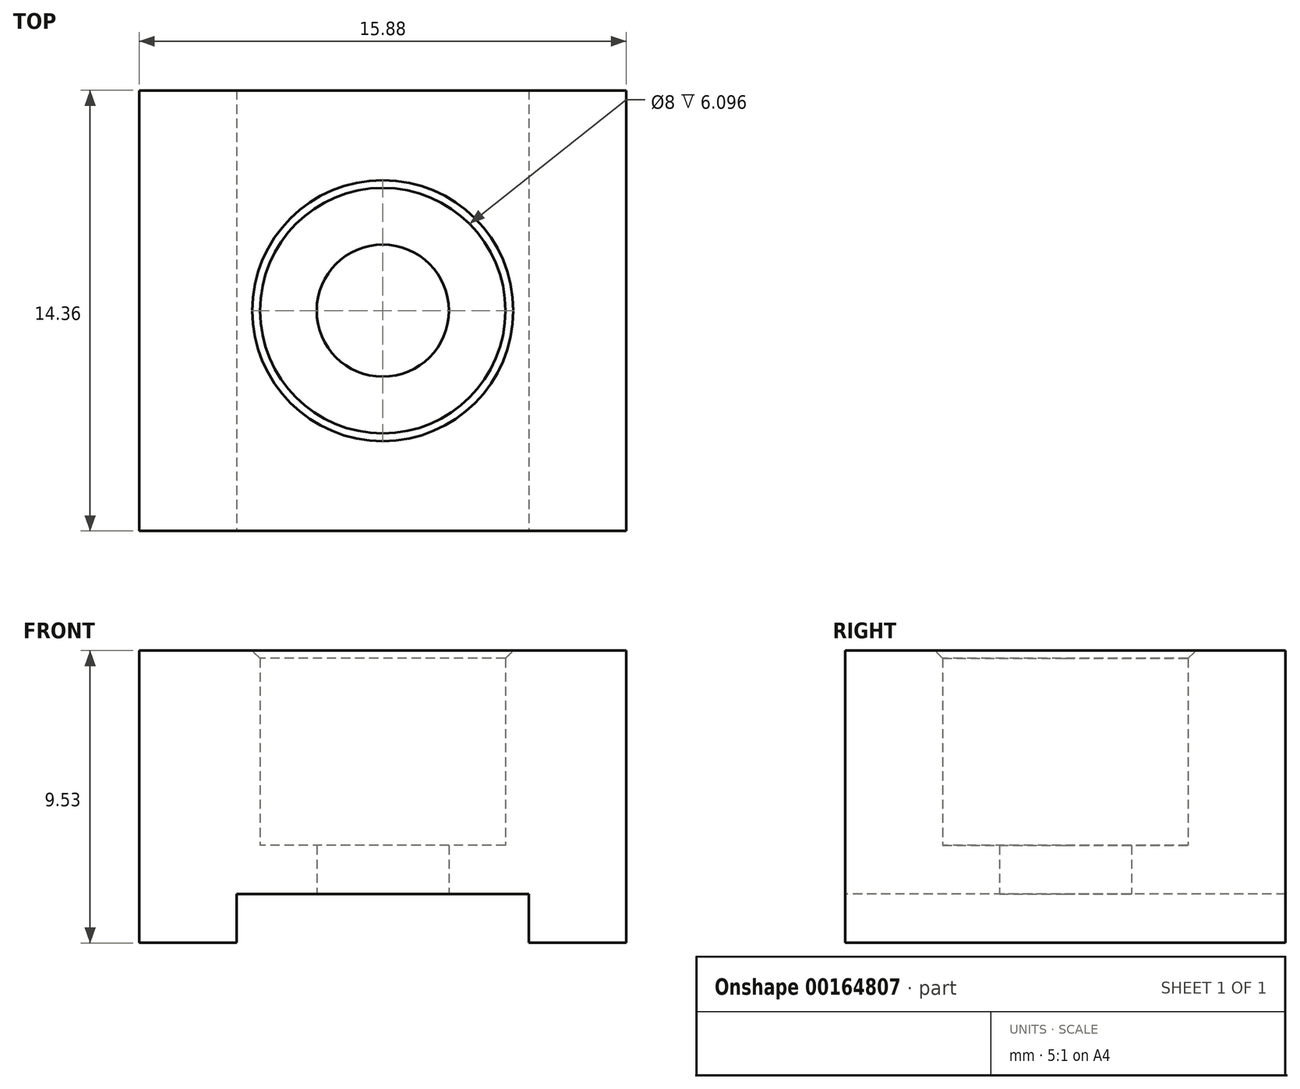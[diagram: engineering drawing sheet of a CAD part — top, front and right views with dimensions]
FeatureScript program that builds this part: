
annotation { "Feature Type Name" : "Feature", "Feature Type Description" : "" }
export const myFeature = defineFeature(function(context is Context, id is Id, definition is map)
    precondition{}
    {
        {
            var Q0;
            Q0=qCreatedBy(makeId("Top.planeOp"),FACE);
            var sketch = newSketch(context, id + "F0", { "sketchPlane" : qUnion([Q0])});
            skLineSegment(sketch, "E0.bottom", {"start": v(7.94, 7.18) * mm, "end": v(-7.94, 7.18) * mm});
            skLineSegment(sketch, "E0.top", {"start": v(7.94, -7.18) * mm, "end": v(-7.94, -7.18) * mm});
            skLineSegment(sketch, "E0.left", {"start": v(7.94, 7.18) * mm, "end": v(7.94, -7.18) * mm});
            skLineSegment(sketch, "E0.right", {"start": v(-7.94, 7.18) * mm, "end": v(-7.94, -7.18) * mm});
            skPoint(sketch, "E0.middle", {"position": v(0, 0) * mm});
            skCircle(sketch, "E1", {"center": v(0, 0) * mm, "radius": 2.15 * mm});
            skSolve(sketch);
        }
        {
            var Q0;
            Q0 = qSketchRegion(id + "F0", true);
            extrude(context, id + "F1", {"entities" : qUnion([Q0]), "depth" : 1.59 * mm});
        }
        {
            var Q0;
            Q0=makeQuery(id+"F1.opExtrude","CAP_FACE",FACE,{"disambiguationData":[OSD([sQuery(id+"F0.wireOp",EDGE,"E0.bottom"),sQuery(id+"F0.wireOp",EDGE,"E0.top"),sQuery(id+"F0.wireOp",EDGE,"E0.left"),sQuery(id+"F0.wireOp",EDGE,"E0.right"),sQuery(id+"F0.wireOp",EDGE,"E1")])],"isStart":false});
            var sketch = newSketch(context, id + "F2", { "sketchPlane" : qUnion([Q0])});
            skCircle(sketch, "E2", {"center": v(0, 0) * mm, "radius": 4 * mm});
            skLineSegment(sketch, "E3.bottom", {"start": v(-7.94, -7.18) * mm, "end": v(7.94, -7.18) * mm});
            skLineSegment(sketch, "E3.top", {"start": v(-7.94, 7.18) * mm, "end": v(7.94, 7.18) * mm});
            skLineSegment(sketch, "E3.left", {"start": v(-7.94, -7.18) * mm, "end": v(-7.94, 7.18) * mm});
            skLineSegment(sketch, "E3.right", {"start": v(7.94, -7.18) * mm, "end": v(7.94, 7.18) * mm});
            skSolve(sketch);
        }
        {
            var Q0;
            Q0 = qSketchRegion(id + "F2", true);
            extrude(context, id + "F3", {"entities" : qUnion([Q0]), "operationType" : NewBodyOperationType.ADD, "depth" : 6.35 * mm});
        }
        {
            var Q0;
            Q0=makeQuery(id+"F3.opExtrude","CAP_EDGE",EDGE,{"disambiguationData":[OSD([sQuery(id+"F2.wireOp",EDGE,"E2")])],"isStart":false});
            chamfer(context, id + "F4", {"entities" : qUnion([Q0]), "width" : 0.25 * mm, "tangentPropagation" : true});
        }
        {
            var Q0;
            Q0=makeQuery(id+"F1.opExtrude","CAP_FACE",FACE,{"disambiguationData":[OSD([sQuery(id+"F0.wireOp",EDGE,"E0.bottom"),sQuery(id+"F0.wireOp",EDGE,"E0.top"),sQuery(id+"F0.wireOp",EDGE,"E0.left"),sQuery(id+"F0.wireOp",EDGE,"E0.right"),sQuery(id+"F0.wireOp",EDGE,"E1")])],"isStart":true});
            var sketch = newSketch(context, id + "F5", { "sketchPlane" : qUnion([Q0])});
            skCircle(sketch, "E4", {"center": v(0, 0) * mm, "radius": 4.76 * mm, "construction": true});
            skLineSegment(sketch, "E5.bottom", {"start": v(-7.94, -7.18) * mm, "end": v(-4.76, -7.18) * mm});
            skLineSegment(sketch, "E5.top", {"start": v(-7.94, 7.18) * mm, "end": v(-4.76, 7.18) * mm});
            skLineSegment(sketch, "E5.left", {"start": v(-7.94, -7.18) * mm, "end": v(-7.94, 7.18) * mm});
            skLineSegment(sketch, "E5.right", {"start": v(-4.76, -7.18) * mm, "end": v(-4.76, 7.18) * mm});
            skLineSegment(sketch, "E6.bottom", {"start": v(7.94, -7.18) * mm, "end": v(4.76, -7.18) * mm});
            skLineSegment(sketch, "E6.top", {"start": v(7.94, 7.18) * mm, "end": v(4.76, 7.18) * mm});
            skLineSegment(sketch, "E6.left", {"start": v(7.94, -7.18) * mm, "end": v(7.94, 7.18) * mm});
            skLineSegment(sketch, "E6.right", {"start": v(4.76, -7.18) * mm, "end": v(4.76, 7.18) * mm});
            skSolve(sketch);
        }
        {
            var Q0;
            Q0 = qSketchRegion(id + "F5", true);
            extrude(context, id + "F6", {"entities" : qUnion([Q0]), "operationType" : NewBodyOperationType.ADD, "depth" : 1.59 * mm});
        }
    });
